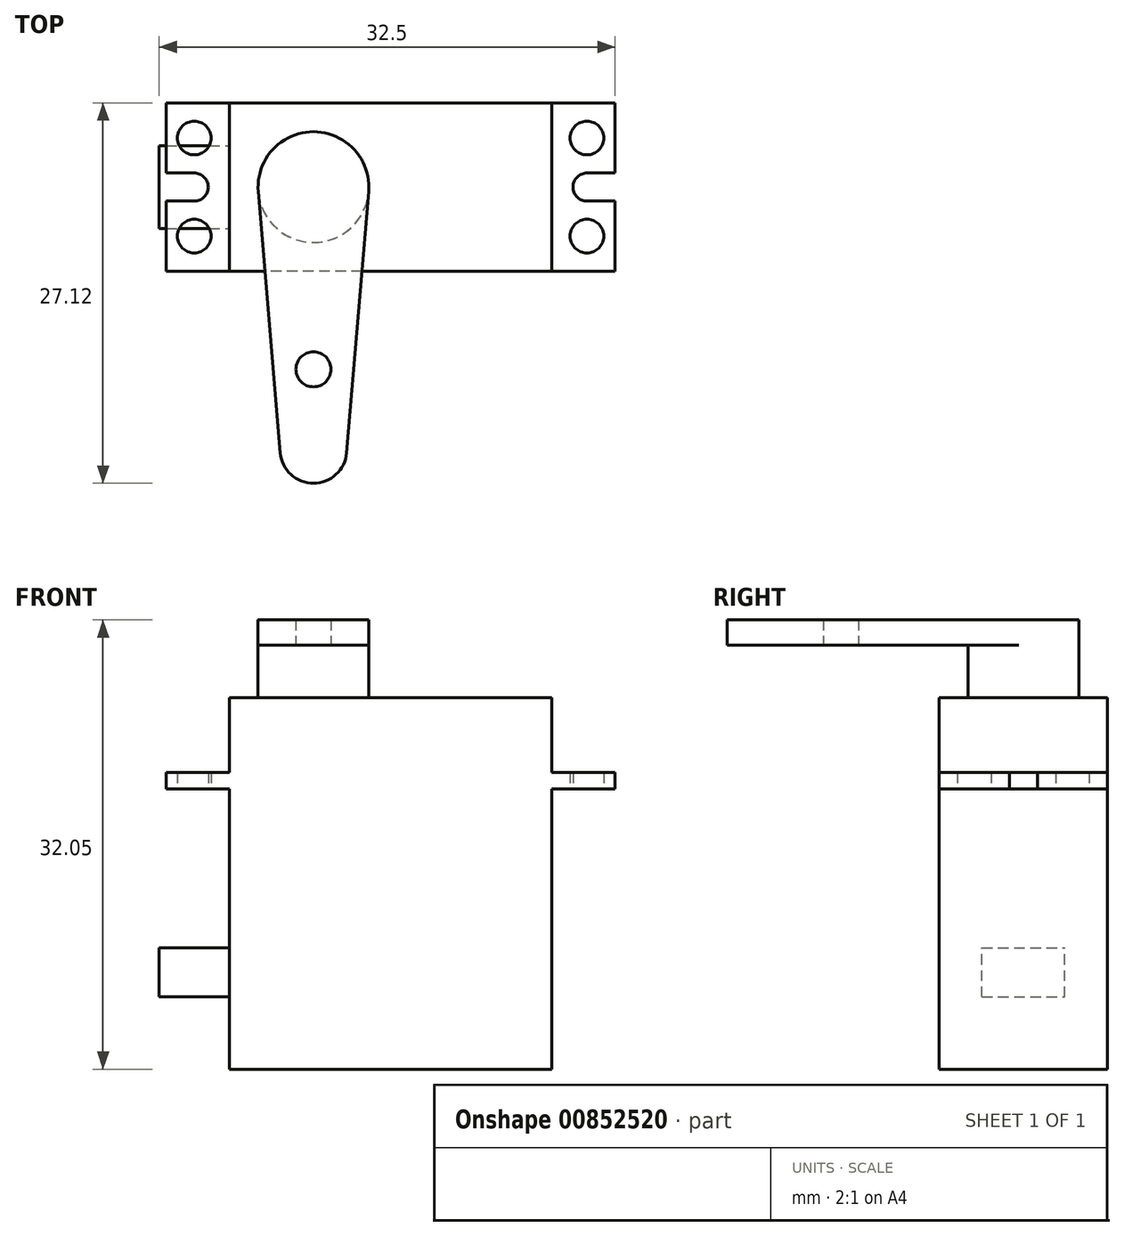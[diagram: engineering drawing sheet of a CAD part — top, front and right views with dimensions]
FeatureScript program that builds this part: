
annotation { "Feature Type Name" : "Feature", "Feature Type Description" : "" }
export const myFeature = defineFeature(function(context is Context, id is Id, definition is map)
    precondition{}
    {
        {
            var Q0;
            Q0=qCreatedBy(makeId("Top.planeOp"),FACE);
            var sketch = newSketch(context, id + "F0", { "sketchPlane" : qUnion([Q0])});
            skLineSegment(sketch, "E0.bottom", {"start": v(11.5, 6) * mm, "end": v(-11.5, 6) * mm});
            skLineSegment(sketch, "E0.top", {"start": v(11.5, -6) * mm, "end": v(-11.5, -6) * mm});
            skLineSegment(sketch, "E0.left", {"start": v(11.5, 6) * mm, "end": v(11.5, -6) * mm});
            skLineSegment(sketch, "E0.right", {"start": v(-11.5, 6) * mm, "end": v(-11.5, -6) * mm});
            skPoint(sketch, "E0.middle", {"position": v(0, 0) * mm});
            skSolve(sketch);
        }
        {
            var Q0;
            Q0=makeQuery(id+"F0.imprint","IMPRINT",FACE,{"disambiguationData":[TD([[makeQuery(id+"F0.imprint","IMPRINT",EDGE,{"derivedFrom":sQuery(id+"F0.wireOp",EDGE,"E0.bottom")}),1.0]])]});
            extrude(context, id + "F1", {"entities" : qUnion([Q0]), "depth" : 26.5 * mm, "offsetDistance" : 25 * mm});
        }
        {
            var Q0;
            Q0=qCreatedBy(makeId("Top.planeOp"),FACE);
            cPlane(context, id + "F2", {"entities" : qUnion([Q0]), "cplaneType" : CPlaneType.OFFSET, "offset" : 20 * mm, "width" : 150 * mm, "height" : 150 * mm});
        }
        {
            var Q0;
            Q0=qCreatedBy(id+"F2.planeOp",FACE);
            var sketch = newSketch(context, id + "F3", { "sketchPlane" : qUnion([Q0])});
            skLineSegment(sketch, "E1.0", {"start": v(11.5, 6) * mm, "end": v(11.5, -6) * mm, "construction": true});
            skLineSegment(sketch, "E2.bottom", {"start": v(16, 6) * mm, "end": v(-16, 6) * mm});
            skLineSegment(sketch, "E2.top", {"start": v(16, -6) * mm, "end": v(-16, -6) * mm});
            skLineSegment(sketch, "E2.left", {"start": v(16, 6) * mm, "end": v(16, 1) * mm});
            skLineSegment(sketch, "E2.right", {"start": v(-16, 6) * mm, "end": v(-16, 1) * mm});
            skPoint(sketch, "E2.middle", {"position": v(0, 0) * mm});
            skLineSegment(sketch, "E3", {"start": v(14, 3.5) * mm, "end": v(14, -3.5) * mm, "construction": true});
            skPoint(sketch, "E4", {"position": v(14, 0) * mm});
            skLineSegment(sketch, "E5.MirrorCS", {"start": v(-14, 3.5) * mm, "end": v(-14, -3.5) * mm, "construction": true});
            skPoint(sketch, "E6.MirrorP", {"position": v(-14, 0) * mm});
            skArc(sketch, "E7", {"start": v(14, 1) * mm, "mid": v(13, 0) * mm, "end": v(14, -1) * mm});
            skLineSegment(sketch, "E8", {"start": v(14, 1) * mm, "end": v(16, 1) * mm});
            skLineSegment(sketch, "E9", {"start": v(14, -1) * mm, "end": v(16, -1) * mm});
            skLineSegment(sketch, "E10.trimOffspring", {"start": v(16, -1) * mm, "end": v(16, -6) * mm});
            skArc(sketch, "E11.MirrorCS", {"start": v(-14, 1) * mm, "mid": v(-13, 0) * mm, "end": v(-14, -1) * mm});
            skLineSegment(sketch, "E12.MirrorCS", {"start": v(-14, 1) * mm, "end": v(-16, 1) * mm});
            skLineSegment(sketch, "E13.MirrorCS", {"start": v(-14, -1) * mm, "end": v(-16, -1) * mm});
            skLineSegment(sketch, "E14.trimOffspring", {"start": v(-16, -1) * mm, "end": v(-16, -6) * mm});
            skSolve(sketch);
        }
        {
            var Q0;
            Q0=makeQuery(id+"F3.imprint","IMPRINT",FACE,{"disambiguationData":[TD([[makeQuery(id+"F3.imprint","IMPRINT",EDGE,{"derivedFrom":sQuery(id+"F3.wireOp",EDGE,"E2.bottom")}),1.0]])]});
            extrude(context, id + "F4", {"entities" : qUnion([Q0]), "operationType" : NewBodyOperationType.ADD, "depth" : 1.15 * mm, "offsetDistance" : 25 * mm});
        }
        {
            var Q0;
            Q0=sQuery(id+"F3.wireOp",VERTEX,"E5.MirrorCS.start");
            var Q1;
            Q1=sQuery(id+"F3.wireOp",VERTEX,"E5.MirrorCS.end");
            var Q2;
            Q2=sQuery(id+"F3.wireOp",VERTEX,"E3.start");
            var Q3;
            Q3=sQuery(id+"F3.wireOp",VERTEX,"E3.end");
            var Q4;
            Q4=makeQuery(id+"F1.opExtrude","SWEPT_BODY",BODY,{"disambiguationData":[OSD([sQuery(id+"F0.wireOp",EDGE,"E0.bottom"),sQuery(id+"F0.wireOp",EDGE,"E0.top"),sQuery(id+"F0.wireOp",EDGE,"E0.left"),sQuery(id+"F0.wireOp",EDGE,"E0.right")])]});
            hole(context, id + "F5", {"style" : HoleStyle.SIMPLE, "endStyle" : HoleEndStyle.THROUGH, "oppositeDirection" : true, "holeDiameter" : 2.4 * mm, "majorDiameter" : 5 * mm, "isTappedThrough" : true, "tappedDepth" : 12 * mm, "tapClearance" : 3, "locations" : qUnion([Q0, Q1, Q2, Q3]), "scope" : qUnion([Q4])});
        }
        {
            var Q0;
            Q0=makeQuery(id+"F1.opExtrude","CAP_FACE",FACE,{"disambiguationData":[OSD([sQuery(id+"F0.wireOp",EDGE,"E0.bottom"),sQuery(id+"F0.wireOp",EDGE,"E0.top"),sQuery(id+"F0.wireOp",EDGE,"E0.left"),sQuery(id+"F0.wireOp",EDGE,"E0.right")])],"isStart":false});
            var sketch = newSketch(context, id + "F6", { "sketchPlane" : qUnion([Q0])});
            skCircle(sketch, "E15", {"center": v(-5.5, 0) * mm, "radius": 3.95 * mm});
            skLineSegment(sketch, "E16.0", {"start": v(-11.5, 6) * mm, "end": v(-11.5, -6) * mm, "construction": true});
            skPoint(sketch, "E17", {"position": v(-11.5, 0) * mm});
            skSolve(sketch);
        }
        {
            var Q0;
            Q0=makeQuery(id+"F6.imprint","IMPRINT",FACE,{"disambiguationData":[TD([[makeQuery(id+"F6.imprint","IMPRINT",EDGE,{"derivedFrom":sQuery(id+"F6.wireOp",EDGE,"E15")}),1.0]])]});
            extrude(context, id + "F7", {"entities" : qUnion([Q0]), "operationType" : NewBodyOperationType.ADD, "depth" : 3.75 * mm, "offsetDistance" : 25 * mm});
        }
        {
            var Q0;
            Q0=makeQuery(id+"F7.opExtrude","CAP_FACE",FACE,{"disambiguationData":[OSD([sQuery(id+"F6.wireOp",EDGE,"E15")])],"isStart":false});
            var sketch = newSketch(context, id + "F8", { "sketchPlane" : qUnion([Q0])});
            skCircle(sketch, "E18.0", {"center": v(-5.5, 0) * mm, "radius": 3.95 * mm});
            skLineSegment(sketch, "E19", {"start": v(-5.5, 0) * mm, "end": v(-5.5, -18.75) * mm, "construction": true});
            skCircle(sketch, "E20", {"center": v(-5.5, -18.75) * mm, "radius": 2.38 * mm});
            skLineSegment(sketch, "E21", {"start": v(-3.13, -18.95) * mm, "end": v(-1.56, -0.33) * mm});
            skLineSegment(sketch, "E22", {"start": v(-7.87, -18.95) * mm, "end": v(-9.44, -0.33) * mm});
            skCircle(sketch, "E23", {"center": v(-5.5, -13) * mm, "radius": 1.25 * mm});
            skSolve(sketch);
        }
        {
            var Q0;
            Q0 = qSketchRegion(id + "F8", true);
            extrude(context, id + "F9", {"entities" : qUnion([Q0]), "operationType" : NewBodyOperationType.ADD, "depth" : 1.8 * mm, "offsetDistance" : 25 * mm});
        }
        {
            var Q0;
            {var subQ1=sQuery(id+"F0.wireOp",EDGE,"E0.top");var subQ2=sQuery(id+"F0.wireOp",EDGE,"E0.right");var subQ3=sQuery(id+"F0.wireOp",EDGE,"E0.bottom");Q0=makeQuery(id+"F4.boolean.opBoolean","SPLIT",FACE,{"disambiguationData":[TD([makeQuery(id+"F1.opExtrude","CAP_FACE",FACE,{"disambiguationData":[OSD([subQ3,subQ1,sQuery(id+"F0.wireOp",EDGE,"E0.left"),subQ2])],"isStart":true})])],"derivedFrom":makeQuery(id+"F1.opExtrude","SWEPT_FACE",FACE,{"disambiguationData":[OSD([subQ2])]})});}
            var sketch = newSketch(context, id + "F10", { "sketchPlane" : qUnion([Q0])});
            skLineSegment(sketch, "E24.bottom", {"start": v(2.95, 5.15) * mm, "end": v(-2.95, 5.15) * mm});
            skLineSegment(sketch, "E24.top", {"start": v(2.95, 8.65) * mm, "end": v(-2.95, 8.65) * mm});
            skLineSegment(sketch, "E24.left", {"start": v(2.95, 5.15) * mm, "end": v(2.95, 8.65) * mm});
            skLineSegment(sketch, "E24.right", {"start": v(-2.95, 5.15) * mm, "end": v(-2.95, 8.65) * mm});
            skPoint(sketch, "E24.middle", {"position": v(0, 6.9) * mm});
            skSolve(sketch);
        }
        {
            var Q0;
            Q0=makeQuery(id+"F10.imprint","IMPRINT",FACE,{"disambiguationData":[TD([[makeQuery(id+"F10.imprint","IMPRINT",EDGE,{"derivedFrom":sQuery(id+"F10.wireOp",EDGE,"E24.bottom")}),-1.0]])]});
            extrude(context, id + "F11", {"entities" : qUnion([Q0]), "operationType" : NewBodyOperationType.ADD, "depth" : 5 * mm, "offsetDistance" : 25 * mm});
        }
    });
